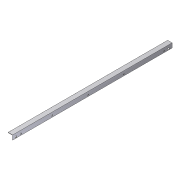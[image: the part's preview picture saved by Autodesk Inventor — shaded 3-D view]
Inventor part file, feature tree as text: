
AUTODESK INVENTOR PART (.ipt)
format: ipt  version: 2012 (Build 160160000, 160)  size: 97,280 bytes
history: native  units: in
note: dims shown in document units (in); Inventor stores cm internally (conversion verified against a paired STEP export)
features: extrude x2, sketch x2
ambient origin geometry x8: Origin, YZ Plane, XZ Plane, XY Plane, X Axis, Y Axis, Z Axis, Center Point
bodies: Solid1 (feature_tree)
feature tree (4):
  extrude  "Extrusion1"  Depth=2.0in
  extrude  "Extrusion2"  Depth=0.125in
  sketch  "Sketch1"  dims[d0=2.0in d1=2.0in]
  sketch  "Sketch2"  dims[d2=0.125in d3=0.125in d4=71.375in d5=0.0in d8=0.8125in d9=0.5625in d12=1.5in d13=1.3125in d14=0.5625in d15=0.5625in d16=0.5625in d17=0.5625in d23=71.375in d24=0.0in d25=0.8125in d26=1.5in d27=1.4688in d28=3.6875in d29=17.6875in d30=33.6875in d31=49.6875in d32=67.6875in d33=69.9063in]
